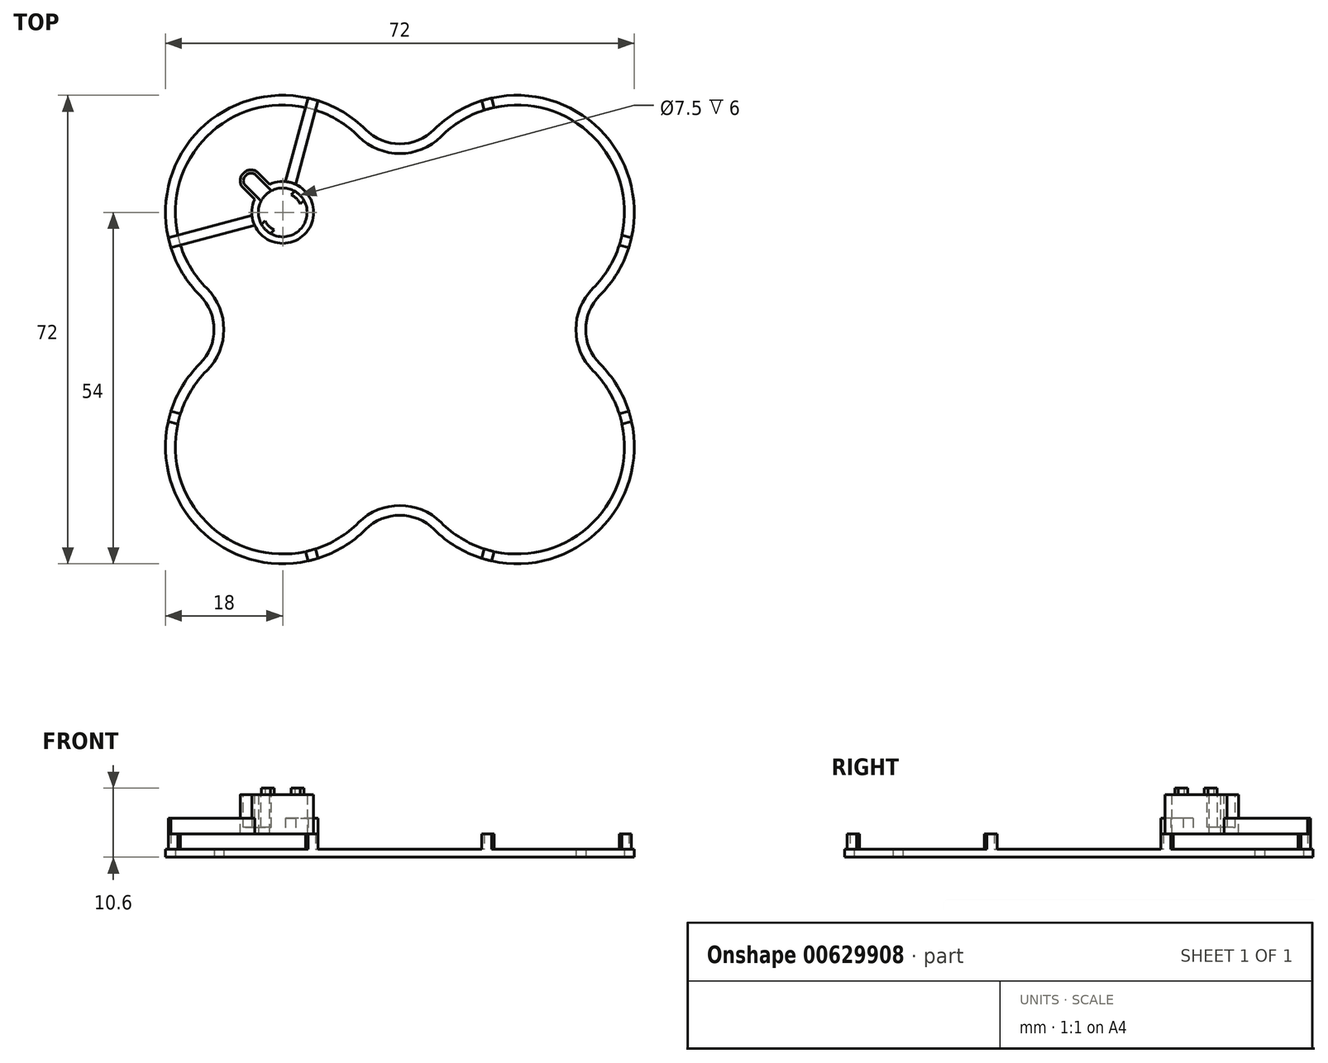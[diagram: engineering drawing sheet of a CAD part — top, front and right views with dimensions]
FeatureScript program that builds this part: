
annotation { "Feature Type Name" : "Feature", "Feature Type Description" : "" }
export const myFeature = defineFeature(function(context is Context, id is Id, definition is map)
    precondition{}
    {
        {
            var Q0;
            Q0=qCreatedBy(makeId("Top.planeOp"),FACE);
            var sketch = newSketch(context, id + "F0", { "sketchPlane" : qUnion([Q0])});
            skArc(sketch, "E0", {"start": v(-30.73, -5.27) * mm, "mid": v(-30.73, -30.73) * mm, "end": v(-5.27, -30.73) * mm});
            skArc(sketch, "E1", {"start": v(-30.73, -5.27) * mm, "mid": v(-28.54, 0) * mm, "end": v(-30.73, 5.27) * mm});
            skArc(sketch, "E2.1.0", {"start": v(5.27, -30.73) * mm, "mid": v(0, -28.54) * mm, "end": v(-5.27, -30.73) * mm});
            skArc(sketch, "E2.2.0", {"start": v(30.73, 5.27) * mm, "mid": v(28.54, 0) * mm, "end": v(30.73, -5.27) * mm});
            skArc(sketch, "E2.3.0", {"start": v(-5.27, 30.73) * mm, "mid": v(0, 28.54) * mm, "end": v(5.27, 30.73) * mm});
            skArc(sketch, "E3.trimOffspring", {"start": v(-5.27, 30.73) * mm, "mid": v(-30.73, 30.73) * mm, "end": v(-30.73, 5.27) * mm});
            skArc(sketch, "E4.trimOffspring", {"start": v(30.73, 5.27) * mm, "mid": v(30.73, 30.73) * mm, "end": v(5.27, 30.73) * mm});
            skArc(sketch, "E5.trimOffspring", {"start": v(5.27, -30.73) * mm, "mid": v(30.73, -30.73) * mm, "end": v(30.73, -5.27) * mm});
            skArc(sketch, "E6.0", {"start": v(-29.67, -6.33) * mm, "mid": v(-29.67, -29.67) * mm, "end": v(-6.33, -29.67) * mm});
            skArc(sketch, "E6.1", {"start": v(6.33, -29.67) * mm, "mid": v(0, -27.04) * mm, "end": v(-6.33, -29.67) * mm});
            skArc(sketch, "E6.2", {"start": v(-29.67, -6.33) * mm, "mid": v(-27.04, 0) * mm, "end": v(-29.67, 6.33) * mm});
            skArc(sketch, "E6.3", {"start": v(6.33, -29.67) * mm, "mid": v(29.67, -29.67) * mm, "end": v(29.67, -6.33) * mm});
            skArc(sketch, "E6.4", {"start": v(-6.33, 29.67) * mm, "mid": v(-29.67, 29.67) * mm, "end": v(-29.67, 6.33) * mm});
            skArc(sketch, "E6.5", {"start": v(-6.33, 29.67) * mm, "mid": v(0, 27.04) * mm, "end": v(6.33, 29.67) * mm});
            skArc(sketch, "E6.6", {"start": v(29.67, 6.33) * mm, "mid": v(29.67, 29.67) * mm, "end": v(6.33, 29.67) * mm});
            skArc(sketch, "E6.7", {"start": v(29.67, 6.33) * mm, "mid": v(27.04, 0) * mm, "end": v(29.67, -6.33) * mm});
            skSolve(sketch);
        }
        {
            var Q0;
            Q0=makeQuery(id+"F0.imprint","IMPRINT",FACE,{"disambiguationData":[TD([[makeQuery(id+"F0.imprint","IMPRINT",EDGE,{"derivedFrom":sQuery(id+"F0.wireOp",EDGE,"E0")}),1.0]])]});
            extrude(context, id + "F1", {"entities" : qUnion([Q0]), "depth" : 1.2 * mm, "offsetDistance" : 25.4 * mm});
        }
        {
            var Q0;
            Q0=makeQuery(id+"F1.opExtrude","CAP_FACE",FACE,{"disambiguationData":[OSD([sQuery(id+"F0.wireOp",EDGE,"E0"),sQuery(id+"F0.wireOp",EDGE,"E1"),sQuery(id+"F0.wireOp",EDGE,"E2.1.0"),sQuery(id+"F0.wireOp",EDGE,"E2.2.0"),sQuery(id+"F0.wireOp",EDGE,"E2.3.0"),sQuery(id+"F0.wireOp",EDGE,"E3.trimOffspring"),sQuery(id+"F0.wireOp",EDGE,"E4.trimOffspring"),sQuery(id+"F0.wireOp",EDGE,"E5.trimOffspring"),sQuery(id+"F0.wireOp",EDGE,"E6.0"),sQuery(id+"F0.wireOp",EDGE,"E6.1"),sQuery(id+"F0.wireOp",EDGE,"E6.2"),sQuery(id+"F0.wireOp",EDGE,"E6.3"),sQuery(id+"F0.wireOp",EDGE,"E6.4"),sQuery(id+"F0.wireOp",EDGE,"E6.5"),sQuery(id+"F0.wireOp",EDGE,"E6.6"),sQuery(id+"F0.wireOp",EDGE,"E6.7")])],"isStart":false});
            var sketch = newSketch(context, id + "F2", { "sketchPlane" : qUnion([Q0])});
            skArc(sketch, "E7.0", {"start": v(-29.67, -6.33) * mm, "mid": v(-29.67, -29.67) * mm, "end": v(-6.33, -29.67) * mm});
            skArc(sketch, "E8.0", {"start": v(-30.73, -5.27) * mm, "mid": v(-30.73, -30.73) * mm, "end": v(-5.27, -30.73) * mm});
            skLineSegment(sketch, "E9.0", {"start": v(-33.71, -12.96) * mm, "end": v(-35.18, -12.57) * mm});
            skLineSegment(sketch, "E10", {"start": v(-35.18, -12.57) * mm, "end": v(-35.6, -14.11) * mm});
            skLineSegment(sketch, "E11", {"start": v(-33.71, -12.96) * mm, "end": v(-34.13, -14.5) * mm});
            skLineSegment(sketch, "E12.0", {"start": v(-12.96, -33.71) * mm, "end": v(-12.57, -35.18) * mm});
            skLineSegment(sketch, "E13", {"start": v(-14.5, -34.13) * mm, "end": v(-12.96, -33.71) * mm});
            skLineSegment(sketch, "E14", {"start": v(-12.57, -35.18) * mm, "end": v(-14.11, -35.6) * mm});
            skLineSegment(sketch, "E15.trimOffspring", {"start": v(-14.5, -34.13) * mm, "end": v(-14.11, -35.6) * mm});
            skLineSegment(sketch, "E16.trimOffspring", {"start": v(-34.13, -14.5) * mm, "end": v(-35.6, -14.11) * mm});
            skLineSegment(sketch, "E17.1.0", {"start": v(14.5, -34.13) * mm, "end": v(14.11, -35.6) * mm});
            skLineSegment(sketch, "E17.1.1", {"start": v(12.96, -33.71) * mm, "end": v(14.5, -34.13) * mm});
            skLineSegment(sketch, "E17.1.2", {"start": v(12.57, -35.18) * mm, "end": v(14.11, -35.6) * mm});
            skLineSegment(sketch, "E17.1.3", {"start": v(12.96, -33.71) * mm, "end": v(12.57, -35.18) * mm});
            skLineSegment(sketch, "E17.1.4", {"start": v(34.13, -14.5) * mm, "end": v(33.71, -12.96) * mm});
            skLineSegment(sketch, "E17.1.5", {"start": v(33.71, -12.96) * mm, "end": v(35.18, -12.57) * mm});
            skLineSegment(sketch, "E17.1.6", {"start": v(35.18, -12.57) * mm, "end": v(35.6, -14.11) * mm});
            skLineSegment(sketch, "E17.1.7", {"start": v(34.13, -14.5) * mm, "end": v(35.6, -14.11) * mm});
            skLineSegment(sketch, "E17.2.0", {"start": v(34.13, 14.5) * mm, "end": v(35.6, 14.11) * mm});
            skLineSegment(sketch, "E17.2.1", {"start": v(33.71, 12.96) * mm, "end": v(34.13, 14.5) * mm});
            skLineSegment(sketch, "E17.2.2", {"start": v(35.18, 12.57) * mm, "end": v(35.6, 14.11) * mm});
            skLineSegment(sketch, "E17.2.3", {"start": v(33.71, 12.96) * mm, "end": v(35.18, 12.57) * mm});
            skLineSegment(sketch, "E17.2.4", {"start": v(14.5, 34.13) * mm, "end": v(12.96, 33.71) * mm});
            skLineSegment(sketch, "E17.2.5", {"start": v(12.96, 33.71) * mm, "end": v(12.57, 35.18) * mm});
            skLineSegment(sketch, "E17.2.6", {"start": v(12.57, 35.18) * mm, "end": v(14.11, 35.6) * mm});
            skLineSegment(sketch, "E17.2.7", {"start": v(14.5, 34.13) * mm, "end": v(14.11, 35.6) * mm});
            skLineSegment(sketch, "E17.3.0", {"start": v(-14.5, 34.13) * mm, "end": v(-14.11, 35.6) * mm});
            skLineSegment(sketch, "E17.3.1", {"start": v(-12.96, 33.71) * mm, "end": v(-14.5, 34.13) * mm});
            skLineSegment(sketch, "E17.3.2", {"start": v(-12.57, 35.18) * mm, "end": v(-14.11, 35.6) * mm});
            skLineSegment(sketch, "E17.3.3", {"start": v(-12.96, 33.71) * mm, "end": v(-12.57, 35.18) * mm});
            skLineSegment(sketch, "E17.3.4", {"start": v(-34.13, 14.5) * mm, "end": v(-33.71, 12.96) * mm});
            skLineSegment(sketch, "E17.3.5", {"start": v(-33.71, 12.96) * mm, "end": v(-35.18, 12.57) * mm});
            skLineSegment(sketch, "E17.3.6", {"start": v(-35.18, 12.57) * mm, "end": v(-35.6, 14.11) * mm});
            skLineSegment(sketch, "E17.3.7", {"start": v(-34.13, 14.5) * mm, "end": v(-35.6, 14.11) * mm});
            skPoint(sketch, "E17.center", {"position": v(0, 0) * mm});
            skSolve(sketch);
        }
        {
            var Q0;
            {var subQ1=sQuery(id+"F2.wireOp",EDGE,"E9.0");var subQ4=sQuery(id+"F2.wireOp",EDGE,"E8.0");var subQ5=makeQuery(id+"F2.imprint","INTERSECT",VERTEX,{"derivedFrom":[subQ4,subQ1]});Q0=makeQuery(id+"F2.imprint","IMPRINT",FACE,{"disambiguationData":[TD([[makeQuery(id+"F2.imprint","IMPRINT",EDGE,{"disambiguationData":[TD([[subQ5,-1.0]])],"derivedFrom":subQ4}),1.0]])]});}
            var Q1;
            {var subQ4=sQuery(id+"F2.wireOp",EDGE,"E8.0");var subQ7=sQuery(id+"F2.wireOp",EDGE,"E15.trimOffspring");var subQ8=makeQuery(id+"F2.imprint","INTERSECT",VERTEX,{"derivedFrom":[subQ4,subQ7]});Q1=makeQuery(id+"F2.imprint","IMPRINT",FACE,{"disambiguationData":[TD([[makeQuery(id+"F2.imprint","IMPRINT",EDGE,{"disambiguationData":[TD([[subQ8,-1.0]])],"derivedFrom":subQ4}),1.0]])]});}
            var Q2;
            {var subQ4=sQuery(id+"F2.wireOp",EDGE,"E17.3.5");var subQ6=makeQuery(id+"F1.opExtrude","CAP_EDGE",EDGE,{"disambiguationData":[OSD([sQuery(id+"F0.wireOp",EDGE,"E3.trimOffspring")])],"isStart":false});var subQ8=makeQuery(id+"F2.imprint","INTERSECT",VERTEX,{"derivedFrom":[subQ6,subQ4]});Q2=makeQuery(id+"F2.imprint","IMPRINT",FACE,{"disambiguationData":[TD([[makeQuery(id+"F2.imprint","IMPRINT",EDGE,{"disambiguationData":[TD([[subQ8,1.0]])],"derivedFrom":subQ6}),1.0]])]});}
            var Q3;
            {var subQ0=sQuery(id+"F2.wireOp",EDGE,"E17.3.0");var subQ1=makeQuery(id+"F1.opExtrude","CAP_EDGE",EDGE,{"disambiguationData":[OSD([sQuery(id+"F0.wireOp",EDGE,"E3.trimOffspring")])],"isStart":false});var subQ2=makeQuery(id+"F2.imprint","INTERSECT",VERTEX,{"derivedFrom":[subQ1,subQ0]});Q3=makeQuery(id+"F2.imprint","IMPRINT",FACE,{"disambiguationData":[TD([[makeQuery(id+"F2.imprint","IMPRINT",EDGE,{"disambiguationData":[TD([[subQ2,1.0]])],"derivedFrom":subQ1}),1.0]])]});}
            var Q4;
            {var subQ0=sQuery(id+"F2.wireOp",EDGE,"E17.2.5");var subQ1=makeQuery(id+"F1.opExtrude","CAP_EDGE",EDGE,{"disambiguationData":[OSD([sQuery(id+"F0.wireOp",EDGE,"E4.trimOffspring")])],"isStart":false});var subQ2=makeQuery(id+"F2.imprint","INTERSECT",VERTEX,{"derivedFrom":[subQ1,subQ0]});Q4=makeQuery(id+"F2.imprint","IMPRINT",FACE,{"disambiguationData":[TD([[makeQuery(id+"F2.imprint","IMPRINT",EDGE,{"disambiguationData":[TD([[subQ2,1.0]])],"derivedFrom":subQ1}),1.0]])]});}
            var Q5;
            {var subQ0=sQuery(id+"F2.wireOp",EDGE,"E17.2.0");var subQ1=makeQuery(id+"F1.opExtrude","CAP_EDGE",EDGE,{"disambiguationData":[OSD([sQuery(id+"F0.wireOp",EDGE,"E4.trimOffspring")])],"isStart":false});var subQ2=makeQuery(id+"F2.imprint","INTERSECT",VERTEX,{"derivedFrom":[subQ1,subQ0]});Q5=makeQuery(id+"F2.imprint","IMPRINT",FACE,{"disambiguationData":[TD([[makeQuery(id+"F2.imprint","IMPRINT",EDGE,{"disambiguationData":[TD([[subQ2,1.0]])],"derivedFrom":subQ1}),1.0]])]});}
            var Q6;
            {var subQ0=sQuery(id+"F2.wireOp",EDGE,"E17.1.5");var subQ1=makeQuery(id+"F1.opExtrude","CAP_EDGE",EDGE,{"disambiguationData":[OSD([sQuery(id+"F0.wireOp",EDGE,"E5.trimOffspring")])],"isStart":false});var subQ2=makeQuery(id+"F2.imprint","INTERSECT",VERTEX,{"derivedFrom":[subQ1,subQ0]});Q6=makeQuery(id+"F2.imprint","IMPRINT",FACE,{"disambiguationData":[TD([[makeQuery(id+"F2.imprint","IMPRINT",EDGE,{"disambiguationData":[TD([[subQ2,1.0]])],"derivedFrom":subQ1}),1.0]])]});}
            var Q7;
            {var subQ0=sQuery(id+"F2.wireOp",EDGE,"E17.1.0");var subQ1=makeQuery(id+"F1.opExtrude","CAP_EDGE",EDGE,{"disambiguationData":[OSD([sQuery(id+"F0.wireOp",EDGE,"E5.trimOffspring")])],"isStart":false});var subQ2=makeQuery(id+"F2.imprint","INTERSECT",VERTEX,{"derivedFrom":[subQ1,subQ0]});Q7=makeQuery(id+"F2.imprint","IMPRINT",FACE,{"disambiguationData":[TD([[makeQuery(id+"F2.imprint","IMPRINT",EDGE,{"disambiguationData":[TD([[subQ2,1.0]])],"derivedFrom":subQ1}),1.0]])]});}
            extrude(context, id + "F3", {"entities" : qUnion([Q0, Q1, Q2, Q3, Q4, Q5, Q6, Q7]), "operationType" : NewBodyOperationType.ADD, "depth" : 2.4 * mm, "offsetDistance" : 25.4 * mm});
        }
        {
            var Q0;
            Q0=makeQuery(id+"F3.opExtrude","CAP_FACE",FACE,{"disambiguationData":[OSD([sQuery(id+"F2.wireOp",EDGE,"E7.0"),sQuery(id+"F2.wireOp",EDGE,"E8.0"),sQuery(id+"F2.wireOp",EDGE,"E12.0"),sQuery(id+"F2.wireOp",EDGE,"E15.trimOffspring")])],"isStart":false});
            var sketch = newSketch(context, id + "F4", { "sketchPlane" : qUnion([Q0])});
            skArc(sketch, "E18.0", {"start": v(-14.5, 34.13) * mm, "mid": v(-29.67, 29.67) * mm, "end": v(-34.13, 14.5) * mm});
            skCircle(sketch, "E19", {"center": v(-18, 18) * mm, "radius": 3.75 * mm});
            skArc(sketch, "E20", {"start": v(-22.32, 16.02) * mm, "mid": v(-14.64, 14.64) * mm, "end": v(-16.02, 22.32) * mm});
            skLineSegment(sketch, "E21.0", {"start": v(-22.73, 17.56) * mm, "end": v(-35.58, 14.12) * mm});
            skLineSegment(sketch, "E22.0", {"start": v(-22.32, 16.02) * mm, "end": v(-35.16, 12.57) * mm});
            skLineSegment(sketch, "E23.0", {"start": v(-17.56, 22.73) * mm, "end": v(-14.12, 35.58) * mm});
            skLineSegment(sketch, "E24.0.0", {"start": v(-12.57, 35.16) * mm, "end": v(-16.02, 22.32) * mm});
            skArc(sketch, "E24.0.1", {"start": v(-12.96, 33.71) * mm, "mid": v(-9.4, 32.09) * mm, "end": v(-6.33, 29.67) * mm});
            skArc(sketch, "E24.0.2", {"start": v(-6.33, 29.67) * mm, "mid": v(0, 27.04) * mm, "end": v(6.33, 29.67) * mm});
            skArc(sketch, "E24.0.3", {"start": v(6.33, 29.67) * mm, "mid": v(9.4, 32.09) * mm, "end": v(12.96, 33.71) * mm});
            skLineSegment(sketch, "E24.0.4", {"start": v(12.96, 33.71) * mm, "end": v(12.57, 35.16) * mm});
            skArc(sketch, "E24.0.5", {"start": v(12.57, 35.16) * mm, "mid": v(8.66, 33.38) * mm, "end": v(5.27, 30.73) * mm});
            skArc(sketch, "E24.0.6", {"start": v(5.27, 30.73) * mm, "mid": v(0, 28.54) * mm, "end": v(-5.27, 30.73) * mm});
            skArc(sketch, "E24.0.7", {"start": v(-5.27, 30.73) * mm, "mid": v(-8.66, 33.38) * mm, "end": v(-12.57, 35.16) * mm});
            skPoint(sketch, "E25.orphan", {"position": v(-34.13, 14.5) * mm});
            skPoint(sketch, "E26.orphan", {"position": v(-33.71, 12.96) * mm});
            skPoint(sketch, "E27.orphan", {"position": v(-14.5, 34.13) * mm});
            skArc(sketch, "E28.trimOffspring", {"start": v(-17.56, 22.73) * mm, "mid": v(-21.36, 21.36) * mm, "end": v(-22.73, 17.56) * mm});
            skLineSegment(sketch, "E29", {"start": v(-35.58, 14.12) * mm, "end": v(-35.16, 12.57) * mm});
            skLineSegment(sketch, "E30", {"start": v(-14.12, 35.58) * mm, "end": v(-12.57, 35.16) * mm});
            skPoint(sketch, "E31.0", {"position": v(0, 0) * mm});
            skSolve(sketch);
        }
        {
            var Q0;
            Q0=makeQuery(id+"F4.imprint","IMPRINT",FACE,{"disambiguationData":[TD([[makeQuery(id+"F4.imprint","IMPRINT",EDGE,{"derivedFrom":sQuery(id+"F4.wireOp",EDGE,"E19")}),-1.0]])]});
            extrude(context, id + "F5", {"entities" : qUnion([Q0]), "operationType" : NewBodyOperationType.ADD, "depth" : 2.4 * mm, "offsetDistance" : 25 * mm});
        }
        {
            var Q0;
            Q0=makeQuery(id+"F5.opExtrude","CAP_FACE",FACE,{"disambiguationData":[OSD([sQuery(id+"F4.wireOp",EDGE,"E19"),sQuery(id+"F4.wireOp",EDGE,"E20"),sQuery(id+"F4.wireOp",EDGE,"E21.0"),sQuery(id+"F4.wireOp",EDGE,"E22.0"),sQuery(id+"F4.wireOp",EDGE,"E23.0"),sQuery(id+"F4.wireOp",EDGE,"E24.0.0"),sQuery(id+"F4.wireOp",EDGE,"E28.trimOffspring"),sQuery(id+"F4.wireOp",EDGE,"E29"),sQuery(id+"F4.wireOp",EDGE,"E30")])],"isStart":false});
            var sketch = newSketch(context, id + "F6", { "sketchPlane" : qUnion([Q0])});
            skArc(sketch, "E32.0", {"start": v(-17.56, 22.73) * mm, "mid": v(-21.36, 21.36) * mm, "end": v(-22.73, 17.56) * mm});
            skCircle(sketch, "E33.0", {"center": v(-18, 18) * mm, "radius": 3.75 * mm});
            skArc(sketch, "E34.0", {"start": v(-22.32, 16.02) * mm, "mid": v(-14.64, 14.64) * mm, "end": v(-16.02, 22.32) * mm});
            skCircle(sketch, "E35", {"center": v(-18, 18) * mm, "radius": 4.75 * mm});
            skSolve(sketch);
        }
        {
            var Q0;
            Q0=makeQuery(id+"F6.imprint","IMPRINT",FACE,{"disambiguationData":[TD([[makeQuery(id+"F6.imprint","IMPRINT",EDGE,{"derivedFrom":sQuery(id+"F6.wireOp",EDGE,"E33.0")}),-1.0]])]});
            extrude(context, id + "F7", {"entities" : qUnion([Q0]), "operationType" : NewBodyOperationType.ADD, "depth" : 3.6 * mm, "offsetDistance" : 25 * mm});
        }
        {
            var Q0;
            Q0=makeQuery(id+"F7.opExtrude","CAP_FACE",FACE,{"disambiguationData":[OSD([sQuery(id+"F6.wireOp",EDGE,"E35"),sQuery(id+"F6.wireOp",EDGE,"E33.0")])],"isStart":false});
            var sketch = newSketch(context, id + "F8", { "sketchPlane" : qUnion([Q0])});
            skLineSegment(sketch, "E36.0", {"start": v(-19.24, 21.54) * mm, "end": v(-21.8, 24.1) * mm});
            skLineSegment(sketch, "E37.0", {"start": v(-21.54, 19.24) * mm, "end": v(-24.1, 21.8) * mm});
            skLineSegment(sketch, "E38", {"start": v(-24.1, 23.92) * mm, "end": v(-23.92, 24.1) * mm});
            skLineSegment(sketch, "E39", {"start": v(-16.85, 19.15) * mm, "end": v(-19.15, 16.85) * mm});
            skPoint(sketch, "E40.visualSharp", {"position": v(-25.16, 22.86) * mm});
            skArc(sketch, "E40.filletArc", {"start": v(-24.1, 23.92) * mm, "mid": v(-24.54, 22.86) * mm, "end": v(-24.1, 21.8) * mm});
            skPoint(sketch, "E41.visualSharp", {"position": v(-22.86, 25.16) * mm});
            skArc(sketch, "E41.filletArc", {"start": v(-21.8, 24.1) * mm, "mid": v(-22.86, 24.54) * mm, "end": v(-23.92, 24.1) * mm});
            skLineSegment(sketch, "E42.0", {"start": v(-21.33, 19.73) * mm, "end": v(-23.75, 22.15) * mm});
            skLineSegment(sketch, "E42.1", {"start": v(-19.73, 21.33) * mm, "end": v(-22.15, 23.75) * mm});
            skArc(sketch, "E42.2", {"start": v(-22.15, 23.75) * mm, "mid": v(-22.86, 24.04) * mm, "end": v(-23.57, 23.75) * mm});
            skLineSegment(sketch, "E42.3", {"start": v(-23.75, 23.57) * mm, "end": v(-23.57, 23.75) * mm});
            skArc(sketch, "E42.4", {"start": v(-23.75, 23.57) * mm, "mid": v(-24.04, 22.86) * mm, "end": v(-23.75, 22.15) * mm});
            skCircle(sketch, "E43.0", {"center": v(-18, 18) * mm, "radius": 4.75 * mm});
            skLineSegment(sketch, "E44", {"start": v(-22.06, 20.47) * mm, "end": v(-22.3, 20) * mm});
            skCircle(sketch, "E45.0", {"center": v(-18, 18) * mm, "radius": 3.75 * mm});
            skLineSegment(sketch, "E46", {"start": v(-19.73, 21.33) * mm, "end": v(-19.24, 21.54) * mm});
            skLineSegment(sketch, "E47", {"start": v(-21.54, 19.24) * mm, "end": v(-21.33, 19.73) * mm});
            skSolve(sketch);
        }
        {
            var Q0;
            Q0=makeQuery(id+"F8.imprint","IMPRINT",FACE,{"disambiguationData":[TD([[makeQuery(id+"F8.imprint","IMPRINT",EDGE,{"derivedFrom":sQuery(id+"F8.wireOp",EDGE,"E38")}),-1.0]])]});
            var Q1;
            Q1=makeQuery(id+"F5.opExtrude","CAP_FACE",FACE,{"disambiguationData":[OSD([sQuery(id+"F4.wireOp",EDGE,"E19"),sQuery(id+"F4.wireOp",EDGE,"E20"),sQuery(id+"F4.wireOp",EDGE,"E21.0"),sQuery(id+"F4.wireOp",EDGE,"E22.0"),sQuery(id+"F4.wireOp",EDGE,"E23.0"),sQuery(id+"F4.wireOp",EDGE,"E24.0.0"),sQuery(id+"F4.wireOp",EDGE,"E28.trimOffspring"),sQuery(id+"F4.wireOp",EDGE,"E29"),sQuery(id+"F4.wireOp",EDGE,"E30")])],"isStart":true});
            extrude(context, id + "F9", {"entities" : qUnion([Q0]), "operationType" : NewBodyOperationType.ADD, "endBound" : BoundingType.UP_TO_SURFACE, "oppositeDirection" : true, "depth" : 25 * mm, "endBoundEntityFace" : qUnion([Q1]), "offsetDistance" : 25 * mm});
        }
        {
            var Q0;
            Q0=makeQuery(id+"F9.boolean.opBoolean","MERGE",FACE,{"derivedFrom":[makeQuery(id+"F7.opExtrude","CAP_FACE",FACE,{"disambiguationData":[OSD([sQuery(id+"F6.wireOp",EDGE,"E35"),sQuery(id+"F6.wireOp",EDGE,"E33.0")])],"isStart":false}),makeQuery(id+"F9.opExtrude","CAP_FACE",FACE,{"disambiguationData":[OSD([sQuery(id+"F8.wireOp",EDGE,"E36.0"),sQuery(id+"F8.wireOp",EDGE,"E37.0"),sQuery(id+"F8.wireOp",EDGE,"E38"),sQuery(id+"F8.wireOp",EDGE,"E40.filletArc"),sQuery(id+"F8.wireOp",EDGE,"E41.filletArc"),sQuery(id+"F8.wireOp",EDGE,"E42.0"),sQuery(id+"F8.wireOp",EDGE,"E42.1"),sQuery(id+"F8.wireOp",EDGE,"E42.2"),sQuery(id+"F8.wireOp",EDGE,"E42.3"),sQuery(id+"F8.wireOp",EDGE,"E42.4"),sQuery(id+"F8.wireOp",EDGE,"E43.0")])],"isStart":true})]});
            var sketch = newSketch(context, id + "F10", { "sketchPlane" : qUnion([Q0])});
            skArc(sketch, "E48.0.0", {"start": v(-22.3, 20) * mm, "mid": v(-14.64, 14.64) * mm, "end": v(-20, 22.3) * mm});
            skLineSegment(sketch, "E48.0.1", {"start": v(-20, 22.3) * mm, "end": v(-21.8, 24.1) * mm});
            skArc(sketch, "E48.0.2", {"start": v(-21.8, 24.1) * mm, "mid": v(-22.86, 24.54) * mm, "end": v(-23.92, 24.1) * mm});
            skLineSegment(sketch, "E48.0.3", {"start": v(-23.92, 24.1) * mm, "end": v(-24.1, 23.92) * mm});
            skArc(sketch, "E48.0.4", {"start": v(-24.1, 23.92) * mm, "mid": v(-24.54, 22.86) * mm, "end": v(-24.1, 21.8) * mm});
            skLineSegment(sketch, "E48.0.5", {"start": v(-24.1, 21.8) * mm, "end": v(-22.3, 20) * mm});
            skSolve(sketch);
        }
        {
            var Q0;
            Q0=makeQuery(id+"F10.imprint","IMPRINT",FACE,{"disambiguationData":[TD([[makeQuery(id+"F10.imprint","IMPRINT",EDGE,{"derivedFrom":sQuery(id+"F10.wireOp",EDGE,"E48.0.0")}),1.0]])]});
            var sketch = newSketch(context, id + "F11", { "sketchPlane" : qUnion([Q0])});
            skCircle(sketch, "E49.0", {"center": v(-18, 18) * mm, "radius": 3.75 * mm});
            skArc(sketch, "E50.0", {"start": v(-20.47, 22.06) * mm, "mid": v(-21.36, 21.36) * mm, "end": v(-22.06, 20.47) * mm});
            skLineSegment(sketch, "E51.0.0", {"start": v(-24.1, 21.8) * mm, "end": v(-22.3, 20) * mm});
            skArc(sketch, "E51.0.1", {"start": v(-22.3, 20) * mm, "mid": v(-14.64, 14.64) * mm, "end": v(-20, 22.3) * mm});
            skLineSegment(sketch, "E51.0.2", {"start": v(-20, 22.3) * mm, "end": v(-21.8, 24.1) * mm});
            skArc(sketch, "E51.0.3", {"start": v(-21.8, 24.1) * mm, "mid": v(-22.86, 24.54) * mm, "end": v(-23.92, 24.1) * mm});
            skLineSegment(sketch, "E51.0.4", {"start": v(-23.92, 24.1) * mm, "end": v(-24.1, 23.92) * mm});
            skArc(sketch, "E51.0.5", {"start": v(-24.1, 23.92) * mm, "mid": v(-24.54, 22.86) * mm, "end": v(-24.1, 21.8) * mm});
            skLineSegment(sketch, "E52", {"start": v(-22.06, 20.47) * mm, "end": v(-21.33, 19.73) * mm});
            skLineSegment(sketch, "E53", {"start": v(-20.47, 22.06) * mm, "end": v(-19.73, 21.33) * mm});
            skArc(sketch, "E54", {"start": v(-21.33, 19.73) * mm, "mid": v(-20.65, 20.65) * mm, "end": v(-19.73, 21.33) * mm});
            skSolve(sketch);
        }
        {
            var Q0;
            Q0=makeQuery(id+"F11.imprint","IMPRINT",FACE,{"disambiguationData":[TD([[makeQuery(id+"F11.imprint","IMPRINT",EDGE,{"derivedFrom":sQuery(id+"F11.wireOp",EDGE,"E50.0")}),1.0]])]});
            extrude(context, id + "F12", {"entities" : qUnion([Q0]), "operationType" : NewBodyOperationType.REMOVE, "oppositeDirection" : true, "depth" : 5 * mm, "offsetDistance" : 25 * mm});
        }
        {
            var Q0;
            {var subQ0=sQuery(id+"F4.wireOp",EDGE,"E30");var subQ1=sQuery(id+"F4.wireOp",EDGE,"E29");var subQ2=sQuery(id+"F4.wireOp",EDGE,"E28.trimOffspring");var subQ3=sQuery(id+"F4.wireOp",EDGE,"E24.0.0");var subQ4=sQuery(id+"F4.wireOp",EDGE,"E23.0");var subQ5=sQuery(id+"F4.wireOp",EDGE,"E22.0");var subQ6=sQuery(id+"F4.wireOp",EDGE,"E21.0");var subQ7=sQuery(id+"F4.wireOp",EDGE,"E20");var subQ8=sQuery(id+"F4.wireOp",EDGE,"E19");Q0=makeQuery(id+"F9.boolean.opBoolean","MERGE",FACE,{"derivedFrom":[makeQuery(id+"F5.opExtrude","CAP_FACE",FACE,{"disambiguationData":[OSD([subQ8,subQ7,subQ6,subQ5,subQ4,subQ3,subQ2,subQ1,subQ0])],"isStart":true}),makeQuery(id+"F9.opExtrude","CAP_FACE",FACE,{"disambiguationData":[OSD([subQ8,subQ7,subQ6,subQ5,subQ4,subQ3,subQ2,subQ1,subQ0])],"isStart":false})]});}
            var sketch = newSketch(context, id + "F13", { "sketchPlane" : qUnion([Q0])});
            skArc(sketch, "E55.0", {"start": v(-23.75, -22.15) * mm, "mid": v(-24.04, -22.86) * mm, "end": v(-23.75, -23.57) * mm});
            skLineSegment(sketch, "E56.0", {"start": v(-23.75, -22.15) * mm, "end": v(-22.06, -20.47) * mm});
            skArc(sketch, "E57.0", {"start": v(-20.47, -22.06) * mm, "mid": v(-21.36, -21.36) * mm, "end": v(-22.06, -20.47) * mm});
            skLineSegment(sketch, "E58.0", {"start": v(-22.15, -23.75) * mm, "end": v(-20.47, -22.06) * mm});
            skArc(sketch, "E59.0", {"start": v(-23.57, -23.75) * mm, "mid": v(-22.86, -24.04) * mm, "end": v(-22.15, -23.75) * mm});
            skLineSegment(sketch, "E60.0", {"start": v(-23.57, -23.75) * mm, "end": v(-23.75, -23.57) * mm});
            skSolve(sketch);
        }
        {
            var Q0;
            Q0=makeQuery(id+"F13.imprint","IMPRINT",FACE,{"disambiguationData":[TD([[makeQuery(id+"F13.imprint","IMPRINT",EDGE,{"derivedFrom":sQuery(id+"F13.wireOp",EDGE,"E55.0")}),1.0]])]});
            extrude(context, id + "F14", {"entities" : qUnion([Q0]), "operationType" : NewBodyOperationType.ADD, "oppositeDirection" : true, "depth" : 1 * mm, "offsetDistance" : 25 * mm});
        }
        {
            var Q0;
            Q0=makeQuery(id+"F10.imprint","IMPRINT",FACE,{"disambiguationData":[TD([[makeQuery(id+"F10.imprint","IMPRINT",EDGE,{"derivedFrom":sQuery(id+"F10.wireOp",EDGE,"E48.0.0")}),1.0]])]});
            var sketch = newSketch(context, id + "F15", { "sketchPlane" : qUnion([Q0])});
            skArc(sketch, "E61.0", {"start": v(-21.33, 19.73) * mm, "mid": v(-21.75, 17.93) * mm, "end": v(-21.26, 16.15) * mm});
            skLineSegment(sketch, "E62.0", {"start": v(-20.58, 14) * mm, "end": v(-19.3, 15.3) * mm});
            skLineSegment(sketch, "E63.0", {"start": v(-22, 15.42) * mm, "end": v(-20.7, 16.7) * mm});
            skArc(sketch, "E64.0", {"start": v(-22.3, 20) * mm, "mid": v(-14.64, 14.64) * mm, "end": v(-20, 22.3) * mm});
            skArc(sketch, "E65.0", {"start": v(-20.7, 16.7) * mm, "mid": v(-20.12, 15.88) * mm, "end": v(-19.3, 15.3) * mm});
            skArc(sketch, "E66.trimOffspring", {"start": v(-15.3, 19.3) * mm, "mid": v(-15.88, 20.12) * mm, "end": v(-16.7, 20.7) * mm});
            skArc(sketch, "E67.trimOffspring", {"start": v(-19.85, 14.74) * mm, "mid": v(-15.35, 15.35) * mm, "end": v(-14.74, 19.85) * mm});
            skArc(sketch, "E68.trimOffspring", {"start": v(-16.15, 21.26) * mm, "mid": v(-17.93, 21.75) * mm, "end": v(-19.73, 21.33) * mm});
            skLineSegment(sketch, "E69.trimOffspring", {"start": v(-15.3, 19.3) * mm, "end": v(-14, 20.58) * mm});
            skLineSegment(sketch, "E70.trimOffspring", {"start": v(-16.7, 20.7) * mm, "end": v(-15.42, 22) * mm});
            skArc(sketch, "E71.0.0", {"start": v(-17.56, 22.73) * mm, "mid": v(-18.81, 22.68) * mm, "end": v(-20, 22.3) * mm});
            skArc(sketch, "E71.0.2", {"start": v(-20, 22.3) * mm, "mid": v(-14.64, 14.64) * mm, "end": v(-22.3, 20) * mm});
            skArc(sketch, "E71.0.4", {"start": v(-22.3, 20) * mm, "mid": v(-22.68, 18.81) * mm, "end": v(-22.73, 17.56) * mm});
            skArc(sketch, "E71.0.6", {"start": v(-22.73, 17.56) * mm, "mid": v(-22.59, 16.77) * mm, "end": v(-22.32, 16.02) * mm});
            skArc(sketch, "E71.0.8", {"start": v(-22.32, 16.02) * mm, "mid": v(-14.64, 14.64) * mm, "end": v(-16.02, 22.32) * mm});
            skArc(sketch, "E71.0.10", {"start": v(-16.02, 22.32) * mm, "mid": v(-16.77, 22.59) * mm, "end": v(-17.56, 22.73) * mm});
            skArc(sketch, "E72", {"start": v(-22, 15.42) * mm, "mid": v(-21.36, 14.64) * mm, "end": v(-20.58, 14) * mm});
            skArc(sketch, "E73", {"start": v(-15.42, 22) * mm, "mid": v(-14.64, 21.36) * mm, "end": v(-14, 20.58) * mm});
            skSolve(sketch);
        }
        {
            var Q0;
            {var subQ0=sQuery(id+"F15.wireOp",EDGE,"E72");Q0=makeQuery(id+"F15.imprint","IMPRINT",FACE,{"disambiguationData":[TD([[makeQuery(id+"F15.imprint","IMPRINT",EDGE,{"derivedFrom":subQ0}),1.0]])]});}
            var Q1;
            {var subQ0=sQuery(id+"F15.wireOp",EDGE,"E66.trimOffspring");Q1=makeQuery(id+"F15.imprint","IMPRINT",FACE,{"disambiguationData":[TD([[makeQuery(id+"F15.imprint","IMPRINT",EDGE,{"derivedFrom":subQ0}),-1.0]])]});}
            var Q2;
            {var subQ0=sQuery(id+"F15.wireOp",EDGE,"E65.0");Q2=makeQuery(id+"F15.imprint","IMPRINT",FACE,{"disambiguationData":[TD([[makeQuery(id+"F15.imprint","IMPRINT",EDGE,{"derivedFrom":subQ0}),-1.0]])]});}
            var Q3;
            {var subQ3=sQuery(id+"F15.wireOp",EDGE,"E73");Q3=makeQuery(id+"F15.imprint","IMPRINT",FACE,{"disambiguationData":[TD([[makeQuery(id+"F15.imprint","IMPRINT",EDGE,{"derivedFrom":subQ3}),1.0]])]});}
            extrude(context, id + "F16", {"entities" : qUnion([Q0, Q1, Q2, Q3]), "operationType" : NewBodyOperationType.ADD, "depth" : 1 * mm, "offsetDistance" : 25 * mm});
        }
        {
            var Q0;
            Q0=qCreatedBy(makeId("Front.planeOp"),FACE);
            var sketch = newSketch(context, id + "F17", { "sketchPlane" : qUnion([Q0])});
            skPoint(sketch, "E74.0", {"position": v(0, 0) * mm});
            skLineSegment(sketch, "E75", {"start": v(0, 0) * mm, "end": v(0, 9.05) * mm});
            skSolve(sketch);
        }
    });
